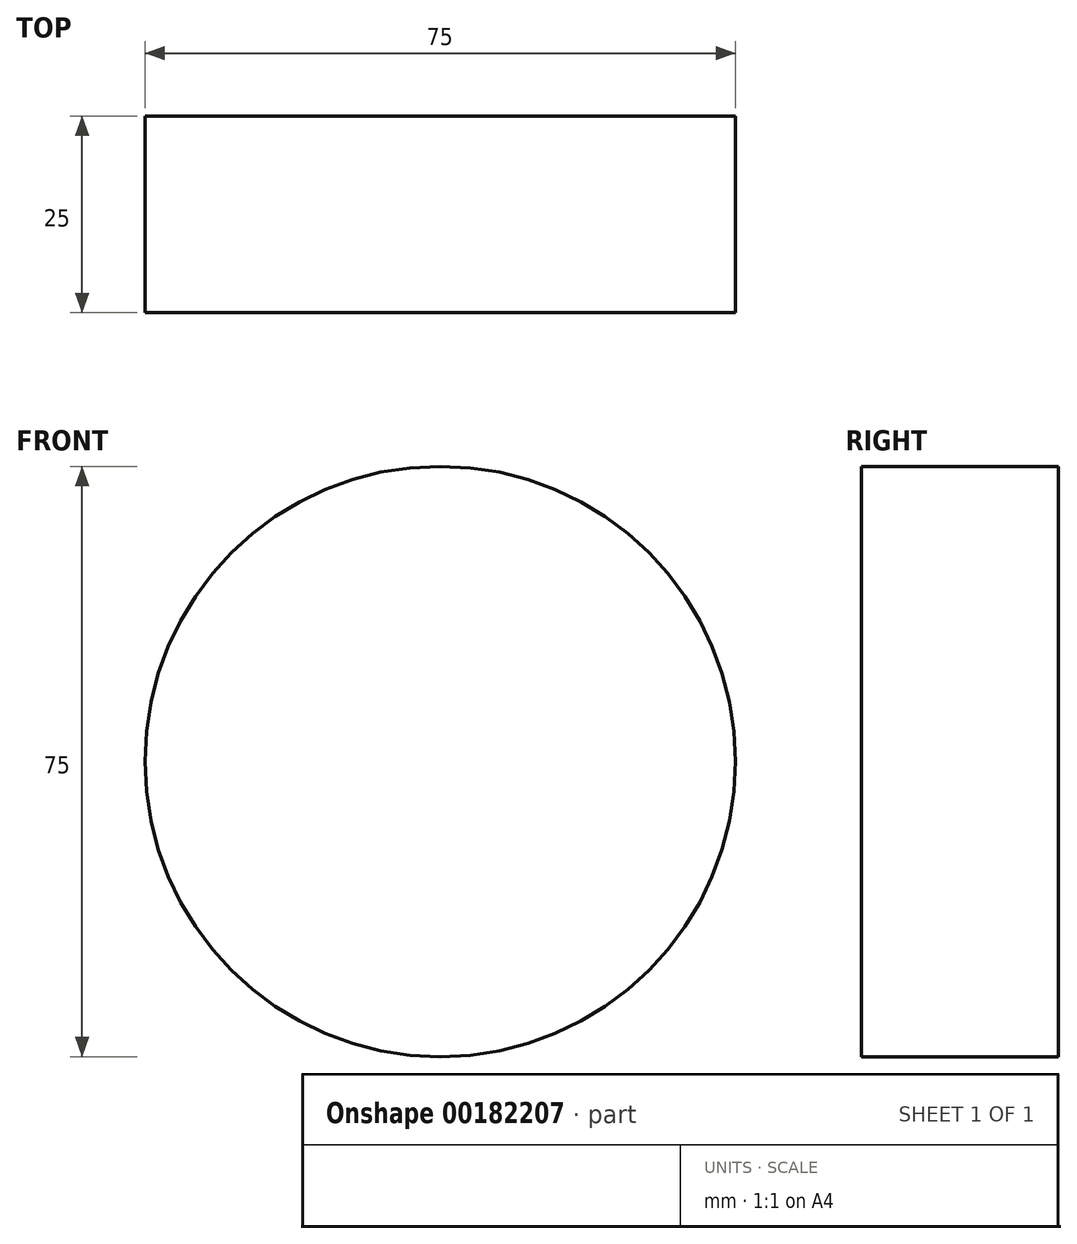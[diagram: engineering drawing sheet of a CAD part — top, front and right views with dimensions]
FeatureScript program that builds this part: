
annotation { "Feature Type Name" : "Feature", "Feature Type Description" : "" }
export const myFeature = defineFeature(function(context is Context, id is Id, definition is map)
    precondition{}
    {
        {
            var Q0;
            Q0=qCreatedBy(makeId("Front.planeOp"),FACE);
            var sketch = newSketch(context, id + "F0", { "sketchPlane" : qUnion([Q0])});
            skCircle(sketch, "E0", {"center": v(0, 0) * mm, "radius": 37.5 * mm});
            skSolve(sketch);
        }
        {
            var Q0;
            Q0=makeQuery(id+"F0.imprint","IMPRINT",FACE,{"disambiguationData":[TD([[makeQuery(id+"F0.imprint","IMPRINT",EDGE,{"derivedFrom":sQuery(id+"F0.wireOp",EDGE,"E0")}),1.0]])]});
            var Q1;
            Q1=sQuery(id+"F0.wireOp",EDGE,"E0");
            extrude(context, id + "F1", {"entities" : qUnion([Q0]), "surfaceEntities" : qUnion([Q1]), "depth" : 25 * mm});
        }
    });
